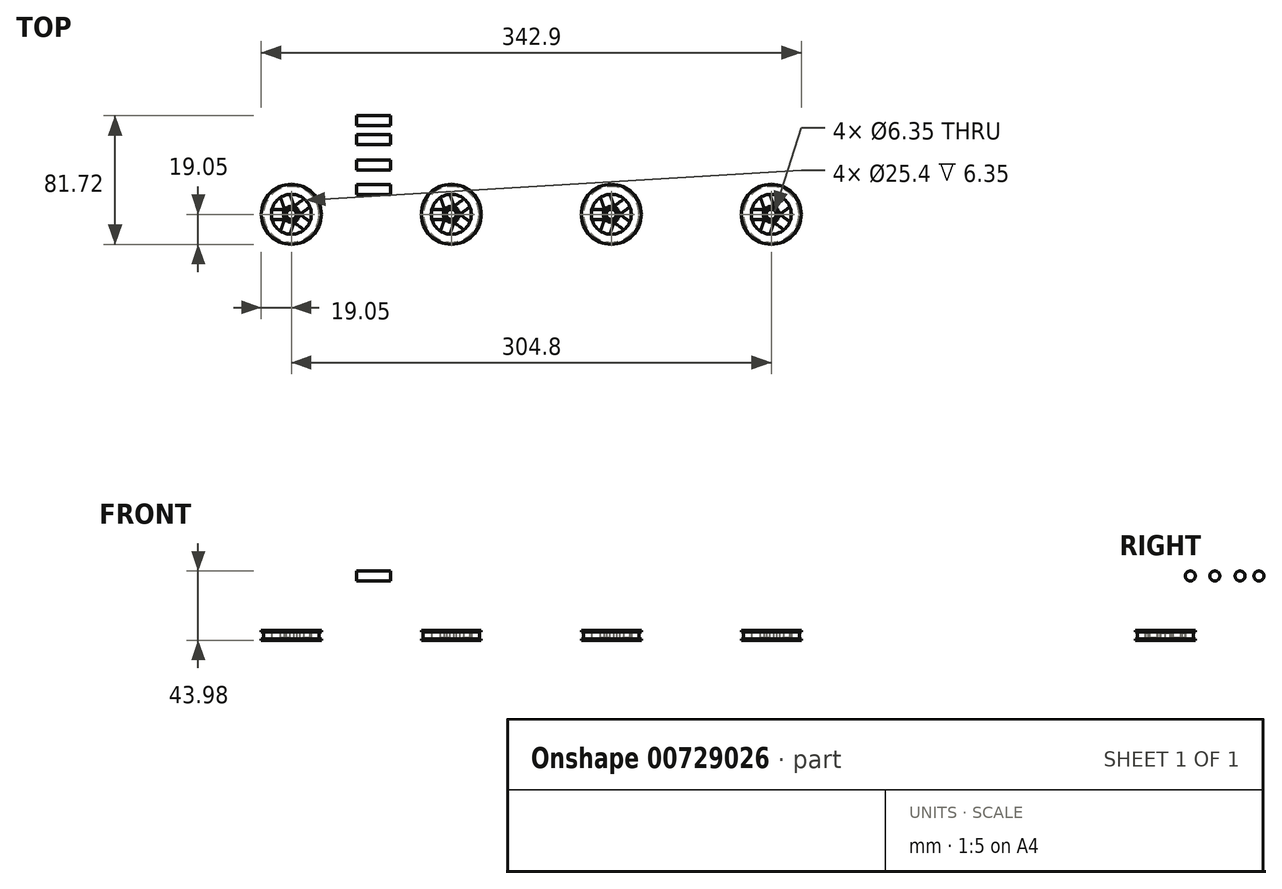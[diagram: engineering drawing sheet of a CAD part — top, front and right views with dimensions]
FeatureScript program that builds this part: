
annotation { "Feature Type Name" : "Feature", "Feature Type Description" : "" }
export const myFeature = defineFeature(function(context is Context, id is Id, definition is map)
    precondition{}
    {
        {
            var Q0;
            Q0=qCreatedBy(makeId("Front.planeOp"),FACE);
            var sketch = newSketch(context, id + "F0", { "sketchPlane" : qUnion([Q0])});
            skLineSegment(sketch, "E0.bottom", {"start": v(-28.82, 5.4) * mm, "end": v(-22.47, 5.4) * mm});
            skLineSegment(sketch, "E0.top", {"start": v(-28.82, -0.95) * mm, "end": v(-22.47, -0.95) * mm});
            skLineSegment(sketch, "E0.left", {"start": v(-28.82, 5.4) * mm, "end": v(-28.82, -0.95) * mm});
            skLineSegment(sketch, "E0.right", {"start": v(-22.47, 5.4) * mm, "end": v(-22.47, -0.95) * mm});
            skLineSegment(sketch, "E1", {"start": v(-22.47, 2.22) * mm, "end": v(-41.52, 2.22) * mm});
            skPoint(sketch, "E2", {"position": v(-38.35, 2.22) * mm});
            skLineSegment(sketch, "E3.bottom", {"start": v(-38.35, -0.95) * mm, "end": v(-36.44, -0.95) * mm});
            skLineSegment(sketch, "E3.top", {"start": v(-38.35, 5.4) * mm, "end": v(-36.44, 5.4) * mm});
            skLineSegment(sketch, "E3.left", {"start": v(-38.35, -0.95) * mm, "end": v(-38.35, 5.4) * mm});
            skLineSegment(sketch, "E3.right", {"start": v(-36.44, -0.95) * mm, "end": v(-36.44, 5.4) * mm});
            skLineSegment(sketch, "E4", {"start": v(-36.44, 3.81) * mm, "end": v(-28.82, 3.81) * mm});
            skLineSegment(sketch, "E5", {"start": v(-36.44, 0.64) * mm, "end": v(-28.82, 0.64) * mm});
            skLineSegment(sketch, "E6", {"start": v(-36.44, 5.4) * mm, "end": v(-28.82, 3.81) * mm});
            skLineSegment(sketch, "E7", {"start": v(-36.44, -0.95) * mm, "end": v(-28.82, 0.63) * mm});
            skLineSegment(sketch, "E8", {"start": v(-41.52, -14.99) * mm, "end": v(-41.52, 19.18) * mm});
            skLineSegment(sketch, "E9", {"start": v(-41.52, 2.22) * mm, "end": v(-60.57, 2.22) * mm});
            skLineSegment(sketch, "E10", {"start": v(-60.57, 4.45) * mm, "end": v(-60.57, 0) * mm});
            skLineSegment(sketch, "E11", {"start": v(-60.57, 4.45) * mm, "end": v(-59.3, 4.45) * mm});
            skLineSegment(sketch, "E12", {"start": v(-59.3, 4.45) * mm, "end": v(-59.3, 0) * mm});
            skLineSegment(sketch, "E13", {"start": v(-59.3, 0) * mm, "end": v(-60.57, 0) * mm});
            skSolve(sketch);
        }
        {
            var Q0;
            Q0=qSketchRegion(id+"F0",true);
            var Q1;
            Q1=sQuery(id+"F0.wireOp",EDGE,"E8");
            revolve(context, id + "F1", {"surfaceOperationType" : NewSurfaceOperationType.NEW, "entities" : qUnion([Q0]), "axis" : qUnion([Q1]), "revolveType" : RevolveType.FULL});
        }
        {
            var Q0;
            Q0=makeQuery(id+"F1.opRevolve","SWEPT_FACE",FACE,{"disambiguationData":[OSD([sQuery(id+"F0.wireOp",EDGE,"E3.top")])]});
            var sketch = newSketch(context, id + "F2", { "sketchPlane" : qUnion([Q0])});
            skCircle(sketch, "E14.cCircle", {"center": v(-41.52, 0) * mm, "radius": 12.7 * mm, "construction": true});
            skLineSegment(sketch, "E14.0", {"start": v(-31.25, 7.46) * mm, "end": v(-31.25, -7.46) * mm});
            skLineSegment(sketch, "E14.1", {"start": v(-31.25, -7.46) * mm, "end": v(-45.44, -12.08) * mm});
            skLineSegment(sketch, "E14.2", {"start": v(-45.44, -12.08) * mm, "end": v(-54.22, 0) * mm});
            skLineSegment(sketch, "E14.3", {"start": v(-54.22, 0) * mm, "end": v(-45.44, 12.08) * mm});
            skLineSegment(sketch, "E14.4", {"start": v(-45.44, 12.08) * mm, "end": v(-31.25, 7.46) * mm});
            skLineSegment(sketch, "E15", {"start": v(-45.44, 12.08) * mm, "end": v(-41.52, 0) * mm});
            skLineSegment(sketch, "E16", {"start": v(-41.52, 0) * mm, "end": v(-31.25, 7.46) * mm});
            skLineSegment(sketch, "E17", {"start": v(-31.25, -7.46) * mm, "end": v(-41.52, 0) * mm});
            skLineSegment(sketch, "E18", {"start": v(-45.44, -12.08) * mm, "end": v(-41.52, 0) * mm});
            skLineSegment(sketch, "E19", {"start": v(-54.22, 0) * mm, "end": v(-41.52, 0) * mm});
            skLineSegment(sketch, "E20", {"start": v(-38.82, 1.96) * mm, "end": v(-46.67, 26.12) * mm});
            skLineSegment(sketch, "E21", {"start": v(-44.86, 0) * mm, "end": v(-53.13, 25.47) * mm});
            skLineSegment(sketch, "E22", {"start": v(-42.55, 3.17) * mm, "end": v(-23.63, 16.92) * mm});
            skLineSegment(sketch, "E23", {"start": v(-38.82, -1.96) * mm, "end": v(-19.38, 12.16) * mm});
            skLineSegment(sketch, "E24", {"start": v(-38.82, 1.96) * mm, "end": v(-17.59, -13.46) * mm});
            skLineSegment(sketch, "E25", {"start": v(-42.55, -3.17) * mm, "end": v(-20.83, -18.95) * mm});
            skLineSegment(sketch, "E26", {"start": v(-38.82, -1.96) * mm, "end": v(-46.86, -26.71) * mm});
            skLineSegment(sketch, "E27", {"start": v(-44.86, 0) * mm, "end": v(-53.31, -26.02) * mm});
            skLineSegment(sketch, "E28", {"start": v(-42.55, 3.17) * mm, "end": v(-68.13, 3.17) * mm});
            skLineSegment(sketch, "E29", {"start": v(-42.55, -3.17) * mm, "end": v(-68.29, -3.17) * mm});
            skCircle(sketch, "E30", {"center": v(-41.52, 0) * mm, "radius": 12.7 * mm});
            skSolve(sketch);
        }
        {
            var Q0;
            {var subQ0=sQuery(id+"F2.wireOp",EDGE,"E20");var subQ1=sQuery(id+"F2.wireOp",EDGE,"E14.4");var subQ2=makeQuery(id+"F2.imprint","INTERSECT",VERTEX,{"derivedFrom":[subQ1,subQ0]});Q0=makeQuery(id+"F2.imprint","IMPRINT",FACE,{"disambiguationData":[TD([[makeQuery(id+"F2.imprint","IMPRINT",EDGE,{"disambiguationData":[TD([[subQ2,-1.0]])],"derivedFrom":subQ1}),1.0]])]});}
            var Q1;
            {var subQ0=sQuery(id+"F2.wireOp",EDGE,"E20");var subQ1=sQuery(id+"F2.wireOp",EDGE,"E14.4");var subQ2=makeQuery(id+"F2.imprint","INTERSECT",VERTEX,{"derivedFrom":[subQ1,subQ0]});Q1=makeQuery(id+"F2.imprint","IMPRINT",FACE,{"disambiguationData":[TD([[makeQuery(id+"F2.imprint","IMPRINT",EDGE,{"disambiguationData":[TD([[subQ2,-1.0]])],"derivedFrom":subQ1}),-1.0]])]});}
            var Q2;
            {var subQ0=sQuery(id+"F2.wireOp",EDGE,"E28");var subQ1=sQuery(id+"F2.wireOp",EDGE,"E14.3");var subQ2=makeQuery(id+"F2.imprint","INTERSECT",VERTEX,{"derivedFrom":[subQ1,subQ0]});Q2=makeQuery(id+"F2.imprint","IMPRINT",FACE,{"disambiguationData":[TD([[makeQuery(id+"F2.imprint","IMPRINT",EDGE,{"disambiguationData":[TD([[subQ2,-1.0]])],"derivedFrom":subQ1}),1.0]])]});}
            var Q3;
            {var subQ0=sQuery(id+"F2.wireOp",EDGE,"E28");var subQ1=sQuery(id+"F2.wireOp",EDGE,"E14.3");var subQ2=makeQuery(id+"F2.imprint","INTERSECT",VERTEX,{"derivedFrom":[subQ1,subQ0]});Q3=makeQuery(id+"F2.imprint","IMPRINT",FACE,{"disambiguationData":[TD([[makeQuery(id+"F2.imprint","IMPRINT",EDGE,{"disambiguationData":[TD([[subQ2,-1.0]])],"derivedFrom":subQ1}),-1.0]])]});}
            var Q4;
            {var subQ0=sQuery(id+"F2.wireOp",EDGE,"E27");var subQ1=sQuery(id+"F2.wireOp",EDGE,"E14.2");var subQ2=makeQuery(id+"F2.imprint","INTERSECT",VERTEX,{"derivedFrom":[subQ1,subQ0]});Q4=makeQuery(id+"F2.imprint","IMPRINT",FACE,{"disambiguationData":[TD([[makeQuery(id+"F2.imprint","IMPRINT",EDGE,{"disambiguationData":[TD([[subQ2,-1.0]])],"derivedFrom":subQ1}),1.0]])]});}
            var Q5;
            {var subQ0=sQuery(id+"F2.wireOp",EDGE,"E27");var subQ1=sQuery(id+"F2.wireOp",EDGE,"E14.2");var subQ2=makeQuery(id+"F2.imprint","INTERSECT",VERTEX,{"derivedFrom":[subQ1,subQ0]});Q5=makeQuery(id+"F2.imprint","IMPRINT",FACE,{"disambiguationData":[TD([[makeQuery(id+"F2.imprint","IMPRINT",EDGE,{"disambiguationData":[TD([[subQ2,-1.0]])],"derivedFrom":subQ1}),-1.0]])]});}
            var Q6;
            {var subQ0=sQuery(id+"F2.wireOp",EDGE,"E25");var subQ1=sQuery(id+"F2.wireOp",EDGE,"E14.1");var subQ2=makeQuery(id+"F2.imprint","INTERSECT",VERTEX,{"derivedFrom":[subQ1,subQ0]});Q6=makeQuery(id+"F2.imprint","IMPRINT",FACE,{"disambiguationData":[TD([[makeQuery(id+"F2.imprint","IMPRINT",EDGE,{"disambiguationData":[TD([[subQ2,-1.0]])],"derivedFrom":subQ1}),-1.0]])]});}
            var Q7;
            {var subQ0=sQuery(id+"F2.wireOp",EDGE,"E25");var subQ1=sQuery(id+"F2.wireOp",EDGE,"E14.1");var subQ2=makeQuery(id+"F2.imprint","INTERSECT",VERTEX,{"derivedFrom":[subQ1,subQ0]});Q7=makeQuery(id+"F2.imprint","IMPRINT",FACE,{"disambiguationData":[TD([[makeQuery(id+"F2.imprint","IMPRINT",EDGE,{"disambiguationData":[TD([[subQ2,-1.0]])],"derivedFrom":subQ1}),1.0]])]});}
            var Q8;
            {var subQ0=sQuery(id+"F2.wireOp",EDGE,"E23");var subQ1=sQuery(id+"F2.wireOp",EDGE,"E14.0");var subQ2=makeQuery(id+"F2.imprint","INTERSECT",VERTEX,{"derivedFrom":[subQ1,subQ0]});Q8=makeQuery(id+"F2.imprint","IMPRINT",FACE,{"disambiguationData":[TD([[makeQuery(id+"F2.imprint","IMPRINT",EDGE,{"disambiguationData":[TD([[subQ2,-1.0]])],"derivedFrom":subQ1}),-1.0]])]});}
            var Q9;
            {var subQ0=sQuery(id+"F2.wireOp",EDGE,"E23");var subQ1=sQuery(id+"F2.wireOp",EDGE,"E14.0");var subQ2=makeQuery(id+"F2.imprint","INTERSECT",VERTEX,{"derivedFrom":[subQ1,subQ0]});Q9=makeQuery(id+"F2.imprint","IMPRINT",FACE,{"disambiguationData":[TD([[makeQuery(id+"F2.imprint","IMPRINT",EDGE,{"disambiguationData":[TD([[subQ2,-1.0]])],"derivedFrom":subQ1}),1.0]])]});}
            extrude(context, id + "F3", {"entities" : qUnion([Q0, Q1, Q2, Q3, Q4, Q5, Q6, Q7, Q8, Q9]), "operationType" : NewBodyOperationType.REMOVE, "oppositeDirection" : true, "depth" : 25.4 * mm, "offsetDistance" : 25.4 * mm});
        }
        {
            var Q0;
            {var subQ5=sQuery(id+"F0.wireOp",EDGE,"E11");Q0=makeQuery(id+"F0.imprint","IMPRINT",FACE,{"disambiguationData":[TD([[makeQuery(id+"F0.imprint","IMPRINT",EDGE,{"derivedFrom":subQ5}),-1.0]])]});}
            var Q1;
            {var subQ5=sQuery(id+"F0.wireOp",EDGE,"E13");Q1=makeQuery(id+"F0.imprint","IMPRINT",FACE,{"disambiguationData":[TD([[makeQuery(id+"F0.imprint","IMPRINT",EDGE,{"derivedFrom":subQ5}),-1.0]])]});}
            var Q2;
            Q2=sQuery(id+"F0.wireOp",EDGE,"E8");
            revolve(context, id + "F4", {"operationType" : NewBodyOperationType.REMOVE, "surfaceOperationType" : NewSurfaceOperationType.NEW, "entities" : qUnion([Q0, Q1]), "axis" : qUnion([Q2]), "revolveType" : RevolveType.FULL, "oppositeDirection" : true});
        }
        {
            var Q0;
            Q0=makeQuery(id+"F1.opRevolve","SWEPT_BODY",BODY,{"disambiguationData":[OSD([sQuery(id+"F0.wireOp",EDGE,"E0.bottom"),sQuery(id+"F0.wireOp",EDGE,"E0.top"),sQuery(id+"F0.wireOp",EDGE,"E0.left"),sQuery(id+"F0.wireOp",EDGE,"E0.right"),sQuery(id+"F0.wireOp",EDGE,"E3.bottom"),sQuery(id+"F0.wireOp",EDGE,"E3.top"),sQuery(id+"F0.wireOp",EDGE,"E3.left"),sQuery(id+"F0.wireOp",EDGE,"E6"),sQuery(id+"F0.wireOp",EDGE,"E7")])]});
            transform(context, id + "F5", {"entities" : qUnion([Q0]), "transformType" : TransformType.TRANSLATION_3D, "dx" : 101.6 * mm, "dy" : 0 * mm, "dz" : 0 * mm, "makeCopy" : true});
        }
        {
            var Q0;
            Q0=makeQuery(id+"F5.opPattern","COPY",BODY,{"derivedFrom":makeQuery(id+"F1.opRevolve","SWEPT_BODY",BODY,{"disambiguationData":[OSD([sQuery(id+"F0.wireOp",EDGE,"E0.bottom"),sQuery(id+"F0.wireOp",EDGE,"E0.top"),sQuery(id+"F0.wireOp",EDGE,"E0.left"),sQuery(id+"F0.wireOp",EDGE,"E0.right"),sQuery(id+"F0.wireOp",EDGE,"E3.bottom"),sQuery(id+"F0.wireOp",EDGE,"E3.top"),sQuery(id+"F0.wireOp",EDGE,"E3.left"),sQuery(id+"F0.wireOp",EDGE,"E6"),sQuery(id+"F0.wireOp",EDGE,"E7")])]}),"instanceName":"1"});
            transform(context, id + "F6", {"entities" : qUnion([Q0]), "transformType" : TransformType.TRANSLATION_3D, "dx" : 101.6 * mm, "dy" : 0 * mm, "dz" : 0 * mm, "makeCopy" : true});
        }
        {
            var Q0;
            Q0=makeQuery(id+"F6.opPattern","COPY",BODY,{"derivedFrom":makeQuery(id+"F5.opPattern","COPY",BODY,{"derivedFrom":makeQuery(id+"F1.opRevolve","SWEPT_BODY",BODY,{"disambiguationData":[OSD([sQuery(id+"F0.wireOp",EDGE,"E0.bottom"),sQuery(id+"F0.wireOp",EDGE,"E0.top"),sQuery(id+"F0.wireOp",EDGE,"E0.left"),sQuery(id+"F0.wireOp",EDGE,"E0.right"),sQuery(id+"F0.wireOp",EDGE,"E3.bottom"),sQuery(id+"F0.wireOp",EDGE,"E3.top"),sQuery(id+"F0.wireOp",EDGE,"E3.left"),sQuery(id+"F0.wireOp",EDGE,"E6"),sQuery(id+"F0.wireOp",EDGE,"E7")])]}),"instanceName":"1"}),"instanceName":"1"});
            transform(context, id + "F7", {"entities" : qUnion([Q0]), "transformType" : TransformType.TRANSLATION_3D, "dx" : 101.6 * mm, "dy" : 0 * mm, "dz" : 0 * mm, "makeCopy" : true});
        }
        {
            var Q0;
            Q0=qCreatedBy(makeId("Right.planeOp"),FACE);
            var sketch = newSketch(context, id + "F8", { "sketchPlane" : qUnion([Q0])});
            skLineSegment(sketch, "E31", {"start": v(59.5, 39.86) * mm, "end": v(15.84, 39.86) * mm});
            skCircle(sketch, "E32", {"center": v(59.5, 39.86) * mm, "radius": 3.18 * mm});
            skCircle(sketch, "E33", {"center": v(47.46, 39.86) * mm, "radius": 3.18 * mm});
            skCircle(sketch, "E34", {"center": v(31.42, 39.86) * mm, "radius": 3.18 * mm});
            skCircle(sketch, "E35", {"center": v(15.84, 39.86) * mm, "radius": 3.18 * mm});
            skSolve(sketch);
        }
        {
            var Q0;
            Q0=qSketchRegion(id+"F8",true);
            extrude(context, id + "F9", {"entities" : qUnion([Q0]), "depth" : 21.59 * mm, "offsetDistance" : 25.4 * mm});
        }
    });
